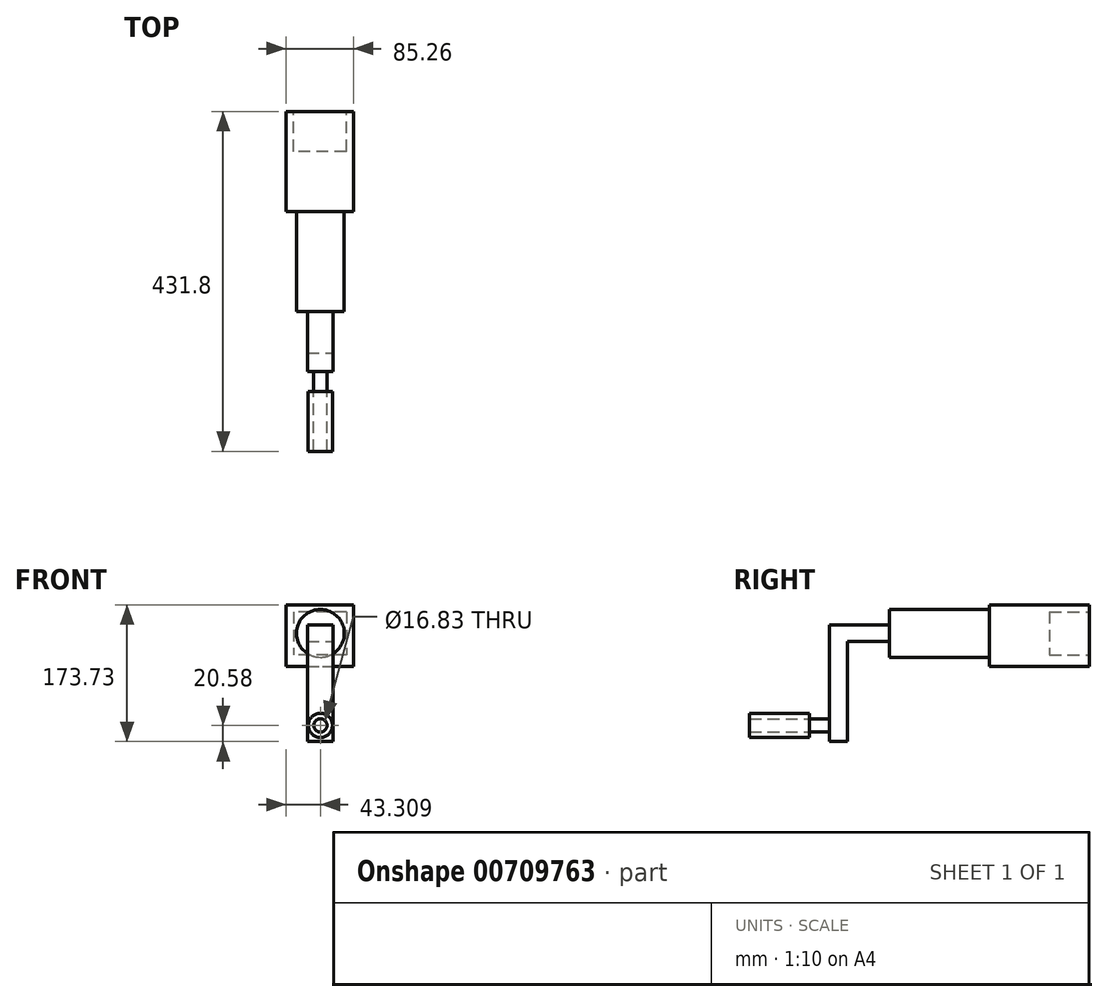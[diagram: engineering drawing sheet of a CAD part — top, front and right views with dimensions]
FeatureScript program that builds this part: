
annotation { "Feature Type Name" : "Feature", "Feature Type Description" : "" }
export const myFeature = defineFeature(function(context is Context, id is Id, definition is map)
    precondition{}
    {
        {
            var Q0;
            Q0=qCreatedBy(makeId("Front.planeOp"),FACE);
            var sketch = newSketch(context, id + "F0", { "sketchPlane" : qUnion([Q0])});
            skLineSegment(sketch, "E0.bottom", {"start": v(-26.94, 36.27) * mm, "end": v(58.32, 36.27) * mm});
            skLineSegment(sketch, "E0.top", {"start": v(-26.94, -41.98) * mm, "end": v(58.32, -41.98) * mm});
            skLineSegment(sketch, "E0.left", {"start": v(-26.94, 36.27) * mm, "end": v(-26.94, -41.98) * mm});
            skLineSegment(sketch, "E0.right", {"start": v(58.32, 36.27) * mm, "end": v(58.32, -41.98) * mm});
            skSolve(sketch);
        }
        {
            var Q0;
            Q0=makeQuery(id+"F0.imprint","IMPRINT",FACE,{"disambiguationData":[TD([[makeQuery(id+"F0.imprint","IMPRINT",EDGE,{"derivedFrom":sQuery(id+"F0.wireOp",EDGE,"E0.bottom")}),-1.0]])]});
            var sketch = newSketch(context, id + "F1", { "sketchPlane" : qUnion([Q0])});
            skCircle(sketch, "E1", {"center": v(16.37, 0) * mm, "radius": 30.37 * mm});
            skSolve(sketch);
        }
        {
            var Q0;
            Q0=makeQuery(id+"F1.imprint","IMPRINT",FACE,{"disambiguationData":[TD([[makeQuery(id+"F1.imprint","IMPRINT",EDGE,{"derivedFrom":sQuery(id+"F1.wireOp",EDGE,"E1")}),1.0]])]});
            extrude(context, id + "F2", {"entities" : qUnion([Q0]), "depth" : 254 * mm, "offsetDistance" : 25.4 * mm});
        }
        {
            var Q0;
            Q0=makeQuery(id+"F0.imprint","IMPRINT",FACE,{"disambiguationData":[TD([[makeQuery(id+"F0.imprint","IMPRINT",EDGE,{"derivedFrom":sQuery(id+"F0.wireOp",EDGE,"E0.bottom")}),-1.0]])]});
            extrude(context, id + "F3", {"entities" : qUnion([Q0]), "operationType" : NewBodyOperationType.ADD, "depth" : 127 * mm, "offsetDistance" : 25.4 * mm});
        }
        {
            var Q0;
            Q0=makeQuery(id+"F2.opExtrude","CAP_FACE",FACE,{"disambiguationData":[OSD([sQuery(id+"F1.wireOp",EDGE,"E1")])],"isStart":false});
            var sketch = newSketch(context, id + "F4", { "sketchPlane" : qUnion([Q0])});
            skLineSegment(sketch, "E2.bottom", {"start": v(0, -10.46) * mm, "end": v(32.74, -10.46) * mm});
            skLineSegment(sketch, "E2.top", {"start": v(0, 10.46) * mm, "end": v(32.74, 10.46) * mm});
            skLineSegment(sketch, "E2.left", {"start": v(0, -10.46) * mm, "end": v(0, 10.46) * mm});
            skLineSegment(sketch, "E2.right", {"start": v(32.74, -10.46) * mm, "end": v(32.74, 10.46) * mm});
            skPoint(sketch, "E2.middle", {"position": v(16.37, 0) * mm});
            skSolve(sketch);
        }
        {
            var Q0;
            Q0=makeQuery(id+"F4.imprint","IMPRINT",FACE,{"disambiguationData":[TD([[makeQuery(id+"F4.imprint","IMPRINT",EDGE,{"derivedFrom":sQuery(id+"F4.wireOp",EDGE,"E2.bottom")}),1.0]])]});
            extrude(context, id + "F5", {"entities" : qUnion([Q0]), "operationType" : NewBodyOperationType.ADD, "depth" : 76.2 * mm, "offsetDistance" : 25.4 * mm});
        }
        {
            var Q0;
            Q0=makeQuery(id+"F5.opExtrude","SWEPT_FACE",FACE,{"disambiguationData":[OSD([sQuery(id+"F4.wireOp",EDGE,"E2.bottom")])]});
            var sketch = newSketch(context, id + "F6", { "sketchPlane" : qUnion([Q0])});
            skLineSegment(sketch, "E3.bottom", {"start": v(0, 330.2) * mm, "end": v(32.74, 330.2) * mm});
            skLineSegment(sketch, "E3.top", {"start": v(0, 307.22) * mm, "end": v(32.74, 307.22) * mm});
            skLineSegment(sketch, "E3.left", {"start": v(0, 330.2) * mm, "end": v(0, 307.22) * mm});
            skLineSegment(sketch, "E3.right", {"start": v(32.74, 330.2) * mm, "end": v(32.74, 307.22) * mm});
            skSolve(sketch);
        }
        {
            var Q0;
            Q0=makeQuery(id+"F6.imprint","IMPRINT",FACE,{"disambiguationData":[TD([[makeQuery(id+"F6.imprint","IMPRINT",EDGE,{"derivedFrom":sQuery(id+"F6.wireOp",EDGE,"E3.bottom")}),-1.0]])]});
            extrude(context, id + "F7", {"entities" : qUnion([Q0]), "operationType" : NewBodyOperationType.ADD, "depth" : 127 * mm, "offsetDistance" : 25.4 * mm});
        }
        {
            var Q0;
            Q0=makeQuery(id+"F7.boolean.opBoolean","MERGE",FACE,{"derivedFrom":[makeQuery(id+"F5.opExtrude","CAP_FACE",FACE,{"disambiguationData":[OSD([sQuery(id+"F4.wireOp",EDGE,"E2.bottom"),sQuery(id+"F4.wireOp",EDGE,"E2.top"),sQuery(id+"F4.wireOp",EDGE,"E2.left"),sQuery(id+"F4.wireOp",EDGE,"E2.right")])],"isStart":false}),makeQuery(id+"F7.opExtrude","SWEPT_FACE",FACE,{"disambiguationData":[OSD([sQuery(id+"F6.wireOp",EDGE,"E3.bottom")])]})]});
            var sketch = newSketch(context, id + "F8", { "sketchPlane" : qUnion([Q0])});
            skCircle(sketch, "E4", {"center": v(16.37, -116.88) * mm, "radius": 8.41 * mm});
            skPoint(sketch, "E4.centerSnap0", {"position": v(16.37, -137.46) * mm});
            skSolve(sketch);
        }
        {
            var Q0;
            Q0=makeQuery(id+"F8.imprint","IMPRINT",FACE,{"disambiguationData":[TD([[makeQuery(id+"F8.imprint","IMPRINT",EDGE,{"derivedFrom":sQuery(id+"F8.wireOp",EDGE,"E4")}),1.0]])]});
            extrude(context, id + "F9", {"entities" : qUnion([Q0]), "operationType" : NewBodyOperationType.ADD, "depth" : 25.4 * mm, "offsetDistance" : 25.4 * mm});
        }
        {
            var Q0;
            Q0=makeQuery(id+"F9.opExtrude","CAP_FACE",FACE,{"disambiguationData":[OSD([sQuery(id+"F8.wireOp",EDGE,"E4")])],"isStart":false});
            var sketch = newSketch(context, id + "F10", { "sketchPlane" : qUnion([Q0])});
            skCircle(sketch, "E5", {"center": v(16.37, -116.88) * mm, "radius": 15.36 * mm});
            skSolve(sketch);
        }
        {
            var Q0;
            Q0=makeQuery(id+"F10.imprint","IMPRINT",FACE,{"disambiguationData":[TD([[makeQuery(id+"F10.imprint","IMPRINT",EDGE,{"derivedFrom":sQuery(id+"F10.wireOp",EDGE,"E5")}),1.0]])]});
            extrude(context, id + "F11", {"entities" : qUnion([Q0]), "depth" : 76.2 * mm, "offsetDistance" : 25.4 * mm});
        }
        {
            var Q0;
            Q0=makeQuery(id+"F3.boolean.opBoolean","MERGE",FACE,{"derivedFrom":[makeQuery(id+"F2.opExtrude","CAP_FACE",FACE,{"disambiguationData":[OSD([sQuery(id+"F1.wireOp",EDGE,"E1")])],"isStart":true}),makeQuery(id+"F3.opExtrude","CAP_FACE",FACE,{"disambiguationData":[OSD([sQuery(id+"F0.wireOp",EDGE,"E0.bottom"),sQuery(id+"F0.wireOp",EDGE,"E0.top"),sQuery(id+"F0.wireOp",EDGE,"E0.left"),sQuery(id+"F0.wireOp",EDGE,"E0.right")])],"isStart":true})]});
            var sketch = newSketch(context, id + "F12", { "sketchPlane" : qUnion([Q0])});
            skLineSegment(sketch, "E6.bottom", {"start": v(-49.37, 27.45) * mm, "end": v(17.98, 27.45) * mm});
            skLineSegment(sketch, "E6.top", {"start": v(-49.37, -27.45) * mm, "end": v(17.98, -27.45) * mm});
            skLineSegment(sketch, "E6.left", {"start": v(-49.37, 27.45) * mm, "end": v(-49.37, -27.45) * mm});
            skLineSegment(sketch, "E6.right", {"start": v(17.98, 27.45) * mm, "end": v(17.98, -27.45) * mm});
            skPoint(sketch, "E6.middle", {"position": v(-15.7, 0) * mm});
            skPoint(sketch, "E6.middle.positionSnap0", {"position": v(-15.7, -41.98) * mm});
            skPoint(sketch, "E6.centerSnap0", {"position": v(-15.7, -41.98) * mm});
            skSolve(sketch);
        }
        {
            var Q0;
            Q0=makeQuery(id+"F12.imprint","IMPRINT",FACE,{"disambiguationData":[TD([[makeQuery(id+"F12.imprint","IMPRINT",EDGE,{"derivedFrom":sQuery(id+"F12.wireOp",EDGE,"E6.bottom")}),-1.0]])]});
            extrude(context, id + "F13", {"entities" : qUnion([Q0]), "operationType" : NewBodyOperationType.REMOVE, "oppositeDirection" : true, "depth" : 50.8 * mm, "offsetDistance" : 25.4 * mm});
        }
    });
